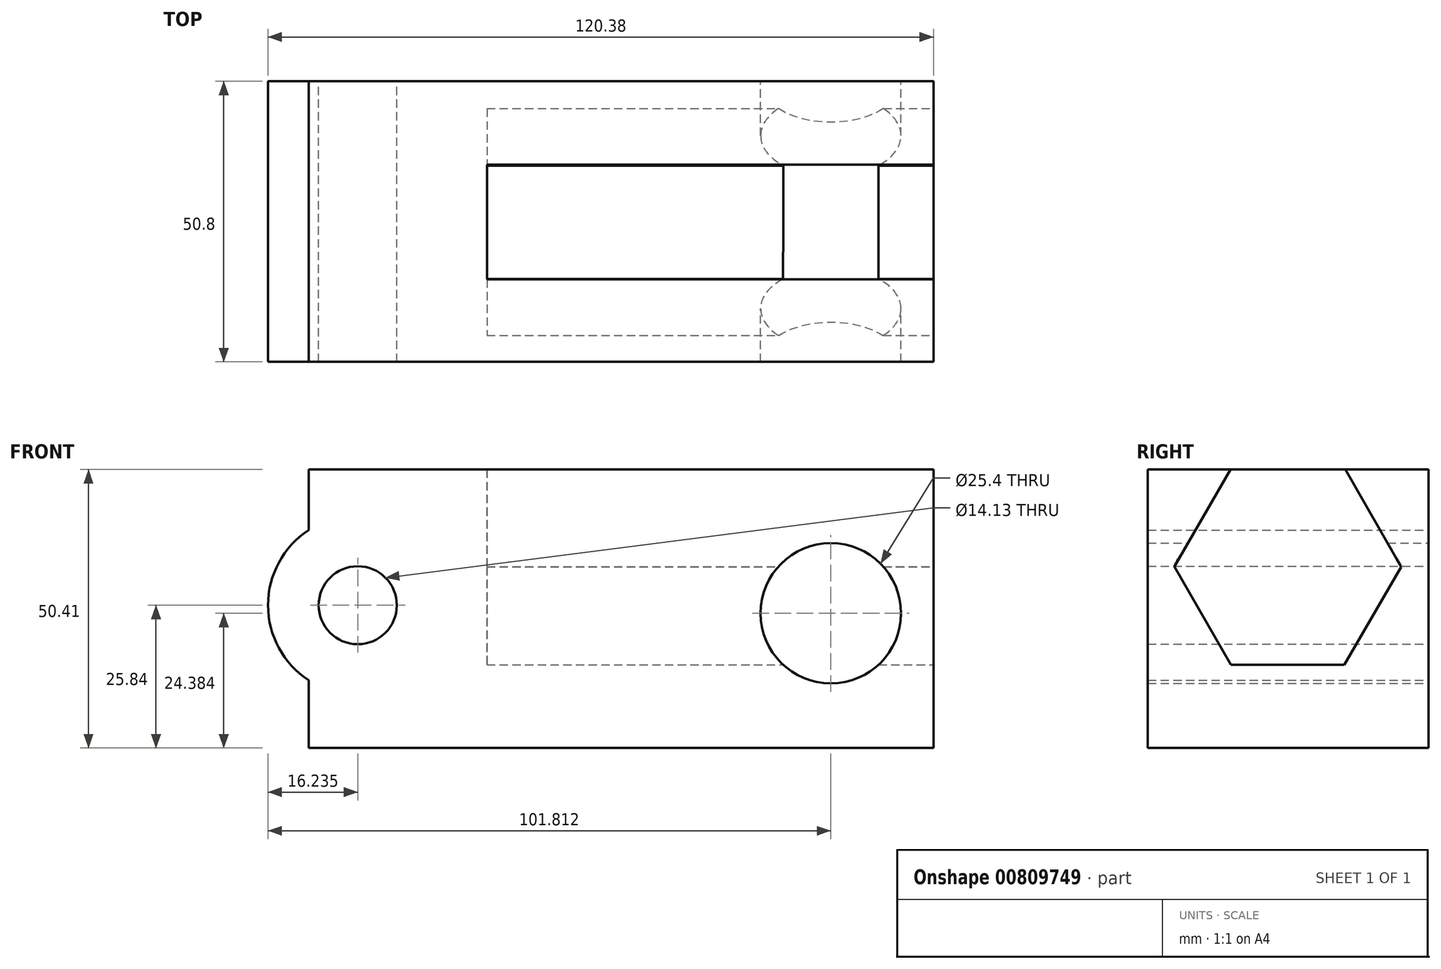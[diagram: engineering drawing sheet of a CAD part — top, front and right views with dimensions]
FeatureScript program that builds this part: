
annotation { "Feature Type Name" : "Feature", "Feature Type Description" : "" }
export const myFeature = defineFeature(function(context is Context, id is Id, definition is map)
    precondition{}
    {
        {
            var Q0;
            Q0=qCreatedBy(makeId("Front.planeOp"),FACE);
            var sketch = newSketch(context, id + "F0", { "sketchPlane" : qUnion([Q0])});
            skLineSegment(sketch, "E0.bottom", {"start": v(-54.33, 24.57) * mm, "end": v(58.7, 24.57) * mm});
            skLineSegment(sketch, "E0.top", {"start": v(-54.33, -25.84) * mm, "end": v(58.7, -25.84) * mm});
            skLineSegment(sketch, "E0.left", {"start": v(-54.33, 24.57) * mm, "end": v(-54.33, -25.84) * mm});
            skLineSegment(sketch, "E0.right", {"start": v(58.7, 24.57) * mm, "end": v(58.7, -25.84) * mm});
            skArc(sketch, "E1", {"start": v(-54.33, 13.59) * mm, "mid": v(-61.68, 0) * mm, "end": v(-54.33, -13.59) * mm});
            skCircle(sketch, "E2", {"center": v(40.13, -1.46) * mm, "radius": 12.7 * mm});
            skCircle(sketch, "E3", {"center": v(-45.44, 0) * mm, "radius": 7.07 * mm});
            skSolve(sketch);
        }
        {
            var Q0;
            Q0 = qSketchRegion(id + "F0", true);
            extrude(context, id + "F1", {"entities" : qUnion([Q0]), "depth" : 50.8 * mm, "offsetDistance" : 25.4 * mm});
        }
        {
            var Q0;
            Q0=makeQuery(id+"F1.opExtrude","SWEPT_FACE",FACE,{"disambiguationData":[OSD([sQuery(id+"F0.wireOp",EDGE,"E0.right")])]});
            var sketch = newSketch(context, id + "F2", { "sketchPlane" : qUnion([Q0])});
            skCircle(sketch, "E4.cCircle", {"center": v(-25.5, 7) * mm, "radius": 17.78 * mm, "construction": true});
            skLineSegment(sketch, "E4.0", {"start": v(-35.8, -10.77) * mm, "end": v(-46.03, 7.03) * mm});
            skLineSegment(sketch, "E4.1", {"start": v(-46.03, 7.03) * mm, "end": v(-35.74, 24.8) * mm});
            skLineSegment(sketch, "E4.2", {"start": v(-35.74, 24.8) * mm, "end": v(-15.2, 24.76) * mm});
            skLineSegment(sketch, "E4.3", {"start": v(-15.2, 24.76) * mm, "end": v(-4.97, 6.96) * mm});
            skLineSegment(sketch, "E4.4", {"start": v(-4.97, 6.96) * mm, "end": v(-15.27, -10.8) * mm});
            skLineSegment(sketch, "E4.5", {"start": v(-15.27, -10.8) * mm, "end": v(-35.8, -10.77) * mm});
            skPoint(sketch, "E4.0.midPoint", {"position": v(-40.91, -1.87) * mm});
            skSolve(sketch);
        }
        {
            var Q0;
            Q0=makeQuery(id+"F2.imprint","IMPRINT",FACE,{"disambiguationData":[TD([[makeQuery(id+"F2.imprint","IMPRINT",EDGE,{"derivedFrom":sQuery(id+"F2.wireOp",EDGE,"E4.0")}),-1.0]])]});
            extrude(context, id + "F3", {"entities" : qUnion([Q0]), "operationType" : NewBodyOperationType.REMOVE, "oppositeDirection" : true, "depth" : 80.77 * mm, "offsetDistance" : 25.4 * mm});
        }
    });
